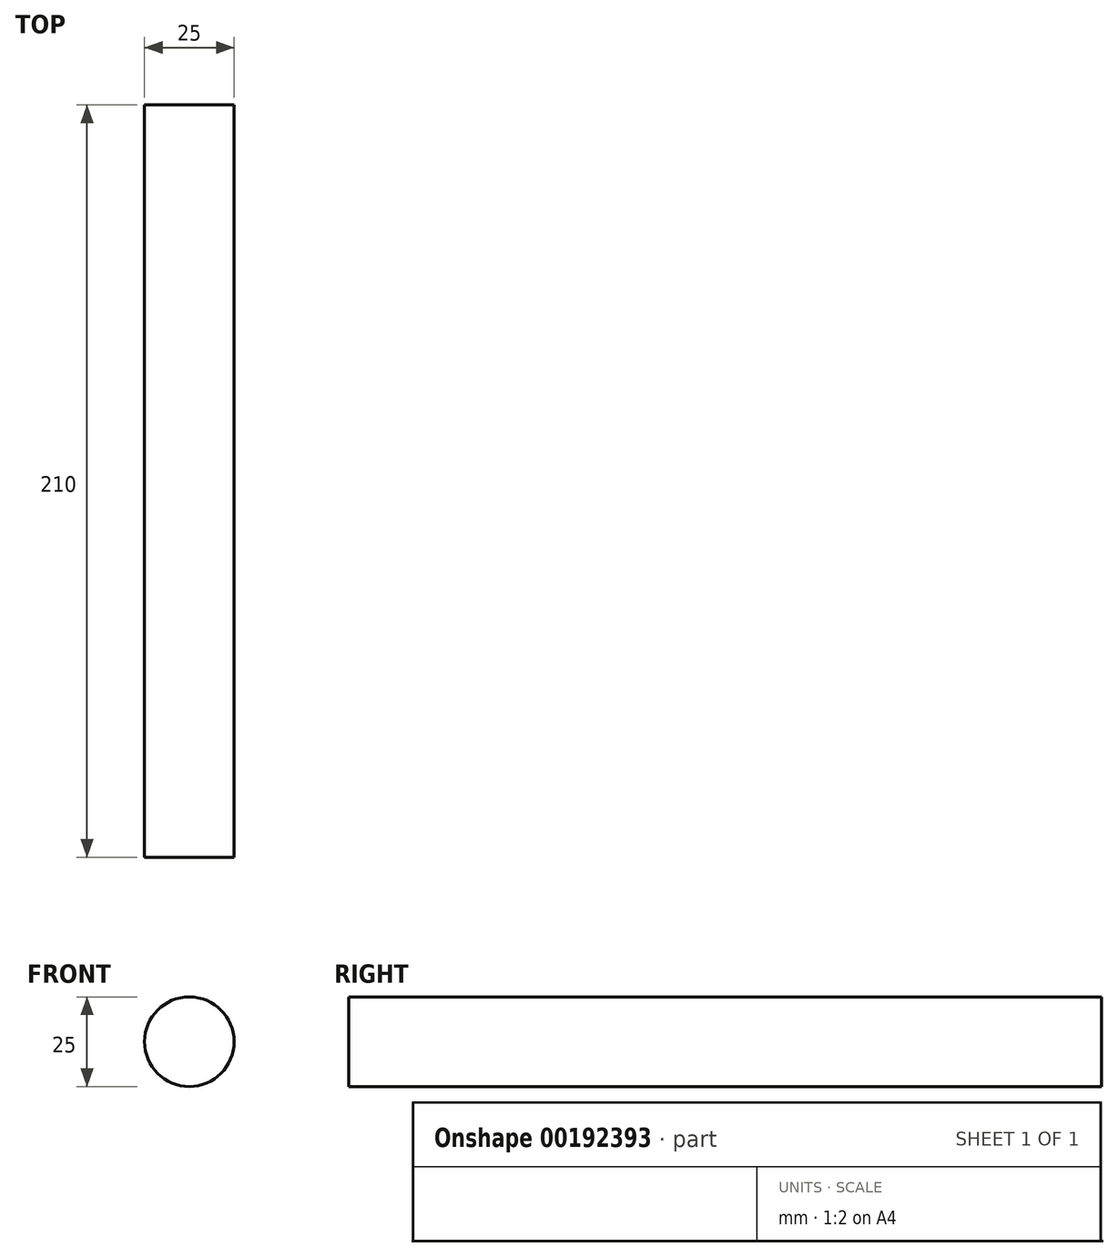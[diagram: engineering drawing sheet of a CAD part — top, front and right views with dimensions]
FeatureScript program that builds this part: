
annotation { "Feature Type Name" : "Feature", "Feature Type Description" : "" }
export const myFeature = defineFeature(function(context is Context, id is Id, definition is map)
    precondition{}
    {
        {
            var Q0;
            Q0=qCreatedBy(makeId("Front.planeOp"),FACE);
            var sketch = newSketch(context, id + "F0", { "sketchPlane" : qUnion([Q0])});
            skCircle(sketch, "E0", {"center": v(0, 0) * mm, "radius": 12.5 * mm});
            skSolve(sketch);
        }
        {
            var Q0;
            Q0 = qSketchRegion(id + "F0", true);
            extrude(context, id + "F1", {"entities" : qUnion([Q0]), "depth" : 210 * mm});
        }
    });
